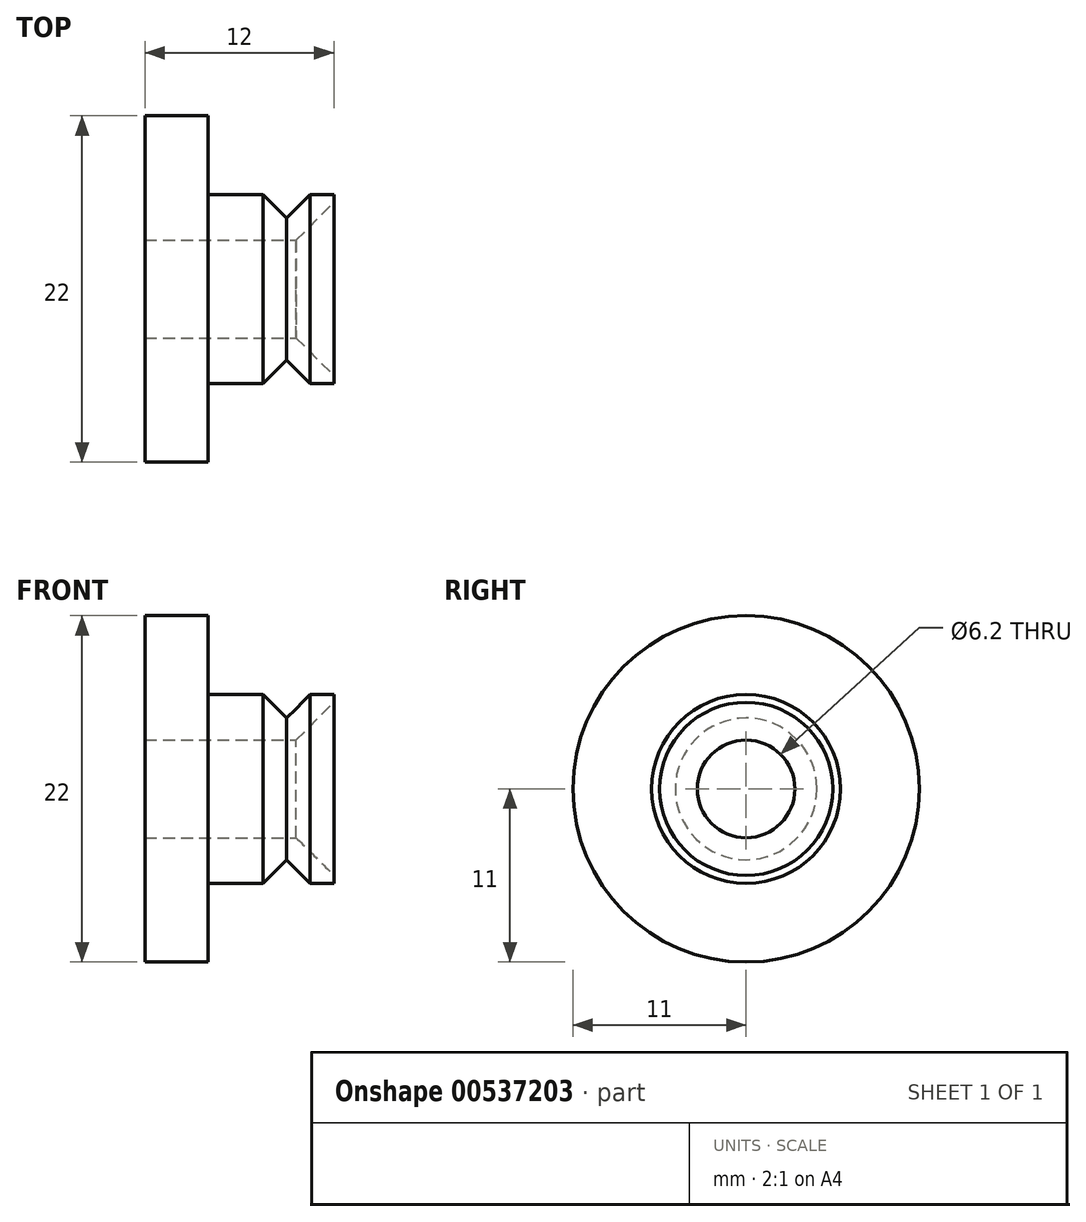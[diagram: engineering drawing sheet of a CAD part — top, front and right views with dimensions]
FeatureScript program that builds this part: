
annotation { "Feature Type Name" : "Feature", "Feature Type Description" : "" }
export const myFeature = defineFeature(function(context is Context, id is Id, definition is map)
    precondition{}
    {
        {
            var Q0;
            Q0=qCreatedBy(makeId("Top.planeOp"),FACE);
            var sketch = newSketch(context, id + "F0", { "sketchPlane" : qUnion([Q0])});
            skLineSegment(sketch, "E0", {"start": v(0, 0) * mm, "end": v(12, 0) * mm});
            skLineSegment(sketch, "E1", {"start": v(12, 0) * mm, "end": v(12, 6) * mm});
            skLineSegment(sketch, "E2", {"start": v(12, 6) * mm, "end": v(10.5, 6) * mm});
            skLineSegment(sketch, "E3", {"start": v(10.5, 6) * mm, "end": v(9, 4.5) * mm});
            skLineSegment(sketch, "E4", {"start": v(9, 4.5) * mm, "end": v(7.5, 6) * mm});
            skLineSegment(sketch, "E5", {"start": v(7.5, 6) * mm, "end": v(4, 6) * mm});
            skLineSegment(sketch, "E6", {"start": v(4, 6) * mm, "end": v(4, 11) * mm});
            skLineSegment(sketch, "E7", {"start": v(4, 11) * mm, "end": v(0, 11) * mm});
            skLineSegment(sketch, "E8", {"start": v(0, 11) * mm, "end": v(0, 0) * mm});
            skSolve(sketch);
        }
        {
            var Q0;
            Q0=makeQuery(id+"F0.imprint","IMPRINT",FACE,{"disambiguationData":[TD([[makeQuery(id+"F0.imprint","IMPRINT",EDGE,{"derivedFrom":sQuery(id+"F0.wireOp",EDGE,"E0")}),1.0]])]});
            var Q1;
            Q1=sQuery(id+"F0.wireOp",EDGE,"E0");
            revolve(context, id + "F1", {"entities" : qUnion([Q0]), "axis" : qUnion([Q1]), "revolveType" : RevolveType.FULL});
        }
        {
            var Q0;
            Q0=makeQuery(id+"F1.opRevolve","SWEPT_FACE",FACE,{"disambiguationData":[OSD([sQuery(id+"F0.wireOp",EDGE,"E1")])]});
            var sketch = newSketch(context, id + "F2", { "sketchPlane" : qUnion([Q0])});
            skPoint(sketch, "E9", {"position": v(0, 0) * mm});
            skSolve(sketch);
        }
        {
            var Q0;
            Q0=sQuery(id+"F2.wireOp",VERTEX,"E9");
            var Q1;
            Q1=makeQuery(id+"F1.opRevolve","SWEPT_BODY",BODY,{"disambiguationData":[OSD([sQuery(id+"F0.wireOp",EDGE,"E0"),sQuery(id+"F0.wireOp",EDGE,"E1"),sQuery(id+"F0.wireOp",EDGE,"E2"),sQuery(id+"F0.wireOp",EDGE,"E3"),sQuery(id+"F0.wireOp",EDGE,"E4"),sQuery(id+"F0.wireOp",EDGE,"E5"),sQuery(id+"F0.wireOp",EDGE,"E6"),sQuery(id+"F0.wireOp",EDGE,"E7"),sQuery(id+"F0.wireOp",EDGE,"E8")])]});
            hole(context, id + "F3", {"style" : HoleStyle.C_SINK, "endStyle" : HoleEndStyle.THROUGH, "holeDiameter" : 6.2 * mm, "cSinkDiameter" : 11 * mm, "cSinkAngle" : 90 * degree, "isTappedThrough" : true, "tappedDepth" : 12 * mm, "tapClearance" : 3, "locations" : qUnion([Q0]), "scope" : qUnion([Q1])});
        }
    });
